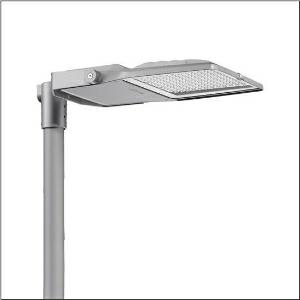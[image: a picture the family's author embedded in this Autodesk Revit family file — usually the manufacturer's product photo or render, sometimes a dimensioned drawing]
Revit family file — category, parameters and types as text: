
# Revit family: floodlight_fl_21_midi___pl61_5xa7785f2c3a_30c2
name_source: partatom
category: Lighting Fixtures
units: mm (PartAtom-declared; Revit-internal decimal feet)

## family parameters
Cut with Voids When Loaded = No
Host = Face
Light Source = No
Part Type = Normal
Room Calculation Point = No
Round Connector Dimension = Use Diameter
Shared = No

## types (1)
- --- (1 x LED, 35100 lm, 271.6 W, 3000K)
    Apparent Load = 272 VA
    CIE Flux Codes = 33 65 98 100 100
    Color Rendering = 70
    Color Temperature = 3000K
    Default Elevation = 1800 mm
    Description = Floodlight FL 21 midi, floodlight, primary light control with lens, of PMMA, primary optical cover: protective disc, of toughened safety glass, transparent, light distribution: PL61, light emission: direct distribution, installation type: surface-mounted, LED, High Power LED, rated luminous flux: 35.100lm, luminous efficacy: 129lm/W, light colour: 730, colour temperature: 3000K, control gear: Smart Interface (Zhaga), control: flexible luminous flux parameterisation, time-dependent luminous flux control, constant luminous flux control, overheat protection, pre-setting: logarithmic dimming characteristic, with terminal, 6-pole, mains connection: 220..240V, AC, 50/60Hz, start of lifetime: 272W, end of service life: 287W, reduction: 123W, luminaire housing, of diecast aluminium, powder-coated, Siteco® metallic grey (DB 702S), corrosivity category C5 mid according to DIN EN ISO 12944, suitable for swimming pools, chlorine-resistant, sealing non-destructively replaceable, please order mast flange separately, mast bracket, of steel, galvanised, powder-coated, Siteco® metallic grey (DB 702S), Smart Interface above, protection rating (complete): IP66, insulation class (complete): insulation class II (safety insulation), certification: CE, ENEC, VDE, protection symbol: D, impact resistance: IK08, permissible operating ambient temperature: -40..+40°C, permissible operating ambient temperature for outdoor applications: -40..+50°C, standard: DIN EN 12944, LABS conformity tested according to VDMA 24364:2018-05, packaging unit: 1 piece

Light Distribution: PL61
    Height = 76 mm
    Lamp = 1 x LED
    Lamp Light Flux = 35100 lm
    Lamp Power = 271.6 W
    Lamp count = 1
    Length = 657 mm
    Luminous efficacy = 129 lm/W
    Manufacturer = Siteco
    ModVariant = No
    Model = 5XA7785F2C3A
    Number of Poles = 1
    OnlyDefault = Yes
    Power Factor = 1
    Product Name = Floodlight FL 21 midi | PL61
    Product group = floodlight | pylon annexe
    ProductGroupID = 6201
    Protection Class = Protection class II
    Protection Degree = IP 66
    RLX_Detail_Level = 1
    RLX_Emergency_Light_Flux = 0 lm
    RLX_Emergency_Type = 0
    RLX_Emergency_Type_DB = No
    RlxData = <blob elided: 153673 chars, md5=b24d59f8>
    Socket = socket
    Standby Power = 0 W
    System Light Flux = 35100 lm
    System Power = 272 W
    Type Comments = factory setting: luminous flux: 100 % | dim-lin: 254 | 620 mA
    Type Image = l_1007123.jpg
    URL = http://relux.com
    VarID = @adj_215301
    Voltage = 0 V
    Weight = 0.00 kg
    Width = 442 mm

## geometry (parser evidence)
native form markers: Blend x4, Sweep x11
no freeform markers — native parametric forms only
